# Revit family: Bath-Drop_In-KALLISTA-Perfect-P50047
name_source: partatom
category: Plumbing Fixtures
units: mm (PartAtom-declared; Revit-internal decimal feet)

## family parameters
Cut with Voids When Loaded = No
Host = Face
OmniClass Number = 23.31.15.00
OmniClass Title = Bathtubs
Part Type = Normal
Room Calculation Point = No
Round Connector Dimension = Use Diameter
Shared = No

## types (1)
- 0-White
    ADA Compliant = No
    Assembly Code = D2010500
    CW Connection = No
    Cold Water Inlet = Cold Water Inlet
    Date Modified = 09/28/2023
    Default Elevation = 0"
    Description = Small Rectangular Bathtub
    Drain Included = No
    Finish = Kallista-Acrylic-0-White
    HW Connection = No
    Height = 22"
    Hot Water Inlet = Hot Water Inlet
    Length = 60"
    Manufacturer = Kallista Co.
    Master Format 2014 = 22 41 19
    Master Format 2014 Name = Residential Bathtubs
    Material = Acrylic
    Model = P50047-00-0
    Product Documentation Link = https://resources.kohler.com
    Product Name = Perfect
    Product Page URL = https://www.kallista.com
    Type = 1
    URL = https://www.kallista.com
    Vent Connection = No
    Waste Connection = Yes
    Waste Water Outlet = Waste Water Outlet
    WaterSense Certified = No
    Width = 32"

## geometry (parser evidence)
native form markers: Sweep x6
no freeform markers — native parametric forms only
